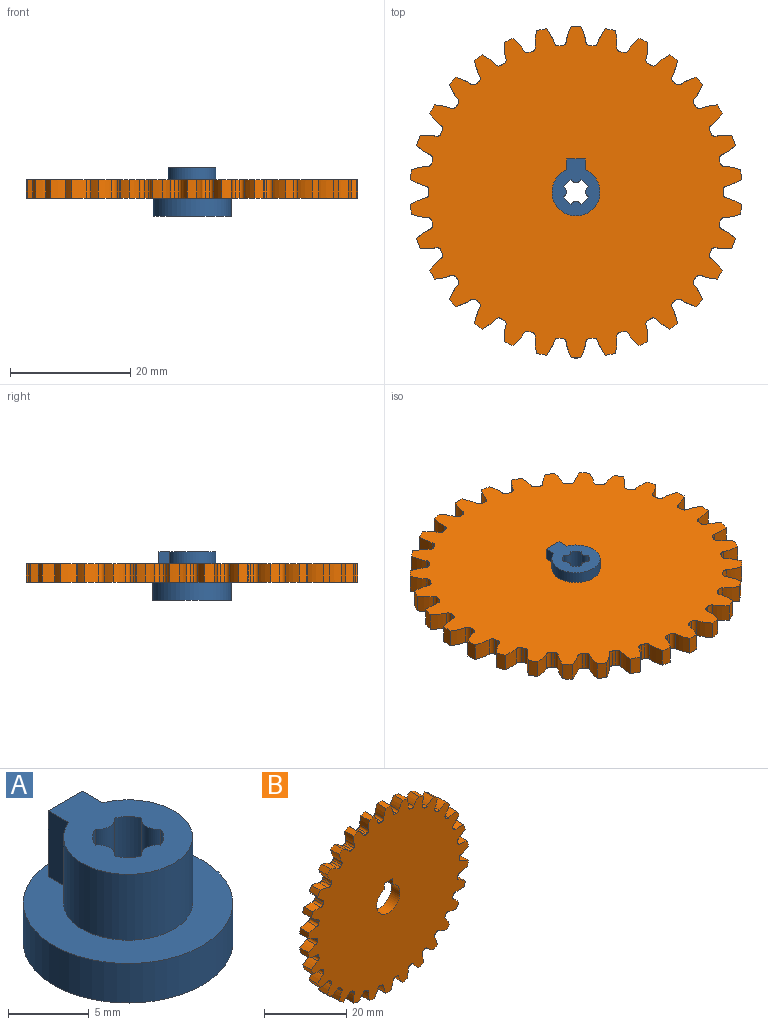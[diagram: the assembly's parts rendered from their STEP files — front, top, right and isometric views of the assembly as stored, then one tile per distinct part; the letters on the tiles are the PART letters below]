
ASSEMBLY  parts=2 mates=1
PART A: 18 faces, bbox 13x13x8 mm
  f0: cylinder r=2.2mm len=6mm, axis (0,0,-1), area 10.6mm2, adj f11,f13,f14,f17
  f1: cylinder r=2.2mm len=6mm, axis (0,0,-1), area 10.6mm2, adj f11,f13,f16,f17
  f2: cylinder r=2.2mm len=6mm, axis (0,0,-1), area 10.6mm2, adj f11,f13,f15,f16
  f3: cylinder r=2.2mm len=6mm, axis (0,0,-1), area 10.6mm2, adj f11,f13,f14,f15
  f4: cylinder r=6.5mm len=13mm, axis (0,0,-1), area 122.5mm2, adj f5,f6
  f5: plane 13x13mm, normal (0,0,1), area 77.7mm2, adj f4,f7,f8,f9,f10
  f6: plane 13x13mm, normal (0,0,-1), area 99.5mm2, adj f4,f12
  f7: cylinder r=4mm len=8mm, axis (0,0,-1), area 110.3mm2, adj f5,f8,f10,f11
  f8: plane 5x1.79mm, normal (1,0,0), area 9mm2, adj f5,f7,f9,f11
  f9: plane 5x3mm, normal (0,1,0), area 15mm2, adj f5,f8,f10,f11
  f10: plane 5x1.79mm, normal (-1,0,0), area 9mm2, adj f5,f7,f9,f11
  f11: plane 9.5x8mm, normal (0,0,1), area 42.6mm2, adj f0,f1,f2,f3,f7,f8,f9,f10
  f12: cylinder r=3.25mm len=6.5mm, axis (0,0,1), area 40.8mm2, adj f6,f13
  f13: plane 6.5x6.5mm, normal (0,0,-1), area 20.7mm2, adj f0,f1,f2,f3,f12,f14,f15,f16
  f14: cylinder r=1mm len=6mm, axis (0,0,1), area 11.7mm2, adj f0,f3,f11,f13
  f15: cylinder r=1mm len=6mm, axis (0,0,1), area 11.7mm2, adj f2,f3,f11,f13
  f16: cylinder r=1mm len=6mm, axis (0,0,1), area 11.7mm2, adj f1,f2,f11,f13
  f17: cylinder r=1mm len=6mm, axis (0,0,1), area 11.7mm2, adj f0,f1,f11,f13
PART B: 186 faces, bbox 55.1x3x55.3 mm
  f0: cylinder r=27.65mm len=3mm, axis (0,1,0), area 4.9mm2, adj f29,f35,f36,f183
  f1: cylinder r=27.65mm len=3mm, axis (0,1,0), area 4.9mm2, adj f29,f35,f178,f181
  f2: cylinder r=27.65mm len=3mm, axis (0,1,0), area 4.9mm2, adj f29,f35,f166,f173
  f3: cylinder r=27.65mm len=3mm, axis (0,1,0), area 4.9mm2, adj f29,f35,f168,f176
  f4: cylinder r=27.65mm len=3mm, axis (0,1,0), area 4.9mm2, adj f29,f35,f163,f171
  f5: cylinder r=27.65mm len=3mm, axis (0,1,0), area 4.9mm2, adj f29,f35,f158,f161
  f6: cylinder r=27.65mm len=3mm, axis (0,1,0), area 4.9mm2, adj f29,f35,f153,f156
  f7: cylinder r=27.65mm len=3mm, axis (0,1,0), area 4.9mm2, adj f29,f35,f148,f151
  f8: cylinder r=27.65mm len=3mm, axis (0,1,0), area 4.9mm2, adj f29,f35,f143,f146
  f9: cylinder r=27.65mm len=3mm, axis (0,1,0), area 4.9mm2, adj f29,f35,f138,f141
  f10: cylinder r=27.65mm len=3mm, axis (0,1,0), area 4.9mm2, adj f29,f35,f126,f133
  f11: cylinder r=27.65mm len=3mm, axis (0,1,0), area 4.9mm2, adj f29,f35,f128,f136
  f12: cylinder r=27.65mm len=3mm, axis (0,1,0), area 4.9mm2, adj f29,f35,f123,f131
  f13: cylinder r=27.65mm len=3mm, axis (0,1,0), area 4.9mm2, adj f29,f35,f118,f121
  f14: cylinder r=27.65mm len=3mm, axis (0,1,0), area 4.9mm2, adj f29,f35,f113,f116
  f15: cylinder r=27.65mm len=3mm, axis (0,1,0), area 4.9mm2, adj f29,f35,f108,f111
  f16: cylinder r=27.65mm len=3mm, axis (0,1,0), area 4.9mm2, adj f29,f35,f96,f103
  f17: cylinder r=27.65mm len=3mm, axis (0,1,0), area 4.9mm2, adj f29,f35,f91,f98
  f18: cylinder r=27.65mm len=3mm, axis (0,1,0), area 4.9mm2, adj f29,f35,f86,f93
  f19: cylinder r=27.65mm len=3mm, axis (0,1,0), area 4.9mm2, adj f29,f35,f88,f106
  f20: cylinder r=27.65mm len=3mm, axis (0,1,0), area 4.9mm2, adj f29,f35,f83,f101
  f21: cylinder r=27.65mm len=3mm, axis (0,1,0), area 4.9mm2, adj f29,f35,f78,f81
  f22: cylinder r=27.65mm len=3mm, axis (0,1,0), area 4.9mm2, adj f29,f35,f73,f76
  f23: cylinder r=27.65mm len=3mm, axis (0,1,0), area 4.9mm2, adj f29,f35,f68,f71
  f24: cylinder r=27.65mm len=3mm, axis (0,1,0), area 4.9mm2, adj f29,f35,f56,f63
  f25: cylinder r=27.65mm len=3mm, axis (0,1,0), area 4.9mm2, adj f29,f35,f51,f58
  f26: cylinder r=27.65mm len=3mm, axis (0,1,0), area 4.9mm2, adj f29,f35,f46,f53
  f27: cylinder r=27.65mm len=3mm, axis (0,1,0), area 4.9mm2, adj f29,f35,f48,f66
  f28: cylinder r=27.65mm len=3mm, axis (0,1,0), area 4.9mm2, adj f29,f35,f43,f61
  f29: plane 55.3x55.15mm, normal (0,-1,0), area 2093.7mm2, adj f0,f1,f2,f3,f4,f5,f6,f7
  f30: plane 3x1.79mm, normal (-1,0,0), area 5.4mm2, adj f29,f31,f33,f35
  f31: cylinder r=4mm len=8mm, axis (0,1,0), area 66.2mm2, adj f29,f30,f32,f35
  f32: plane 3x1.79mm, normal (1,0,0), area 5.4mm2, adj f29,f31,f33,f35
  f33: plane 3x3mm, normal (0,0,-1), area 9mm2, adj f29,f30,f32,f35
  f34: cylinder r=27.65mm len=3mm, axis (0,1,0), area 4.9mm2, adj f29,f35,f38,f41
  f35: plane 55.3x55.15mm, normal (0,1,0), area 2093.7mm2, adj f0,f1,f2,f3,f4,f5,f6,f7
  f36: extruded ~3x2.51mm, area 8.2mm2, adj f0,f29,f35,f39
  f37: cylinder r=24.5mm len=3mm, axis (0,1,0), area 1.6mm2, adj f29,f35,f39,f40
  f38: extruded ~3x2.51mm, area 8.2mm2, adj f29,f34,f35,f40
  f39: cylinder r=0.73mm len=3mm, axis (0,1,0), area 3mm2, adj f29,f35,f36,f37
  f40: cylinder r=0.73mm len=3mm, axis (0,1,0), area 3mm2, adj f29,f35,f37,f38
  f41: extruded ~3x2.68mm, area 8.2mm2, adj f29,f34,f35,f44
  f42: cylinder r=24.5mm len=3mm, axis (0,1,0), area 1.6mm2, adj f29,f35,f44,f45
  f43: extruded ~3x2.23mm, area 8.2mm2, adj f28,f29,f35,f45
  f44: cylinder r=0.73mm len=3mm, axis (0,1,0), area 3mm2, adj f29,f35,f41,f42
  f45: cylinder r=0.73mm len=3mm, axis (0,1,0), area 3mm2, adj f29,f35,f42,f43
  f46: extruded ~3x2.19mm, area 8.2mm2, adj f26,f29,f35,f49
  f47: cylinder r=24.5mm len=3mm, axis (0,1,0), area 1.6mm2, adj f29,f35,f49,f50
  f48: extruded ~3x2.71mm, area 8.2mm2, adj f27,f29,f35,f50
  f49: cylinder r=0.73mm len=3mm, axis (0,1,0), area 3mm2, adj f29,f35,f46,f47
  f50: cylinder r=0.73mm len=3mm, axis (0,1,0), area 3mm2, adj f29,f35,f47,f48
  f51: extruded ~3x2.48mm, area 8.2mm2, adj f25,f29,f35,f54
  f52: cylinder r=24.5mm len=3mm, axis (0,1,0), area 1.6mm2, adj f29,f35,f54,f55
  f53: extruded ~3x2.59mm, area 8.2mm2, adj f26,f29,f35,f55
  f54: cylinder r=0.73mm len=3mm, axis (0,1,0), area 3mm2, adj f29,f35,f51,f52
  f55: cylinder r=0.73mm len=3mm, axis (0,1,0), area 3mm2, adj f29,f35,f52,f53
  f56: extruded ~3x2.67mm, area 8.2mm2, adj f24,f29,f35,f59
  f57: cylinder r=24.5mm len=3mm, axis (0,1,0), area 1.6mm2, adj f29,f35,f59,f60
  f58: extruded ~3x2.35mm, area 8.2mm2, adj f25,f29,f35,f60
  f59: cylinder r=0.73mm len=3mm, axis (0,1,0), area 3mm2, adj f29,f35,f56,f57
  f60: cylinder r=0.73mm len=3mm, axis (0,1,0), area 3mm2, adj f29,f35,f57,f58
  f61: extruded ~3x2.73mm, area 8.2mm2, adj f28,f29,f35,f64
  f62: cylinder r=24.5mm len=3mm, axis (0,1,0), area 1.6mm2, adj f29,f35,f64,f65
  f63: extruded ~3x2.01mm, area 8.2mm2, adj f24,f29,f35,f65
  f64: cylinder r=0.73mm len=3mm, axis (0,1,0), area 3mm2, adj f29,f35,f61,f62
  f65: cylinder r=0.73mm len=3mm, axis (0,1,0), area 3mm2, adj f29,f35,f62,f63
  f66: extruded ~3x2.05mm, area 8.2mm2, adj f27,f29,f35,f69
  f67: cylinder r=24.5mm len=3mm, axis (0,1,0), area 1.6mm2, adj f29,f35,f69,f70
  f68: extruded ~3x2.72mm, area 8.2mm2, adj f23,f29,f35,f70
  f69: cylinder r=0.73mm len=3mm, axis (0,1,0), area 3mm2, adj f29,f35,f66,f67
  f70: cylinder r=0.73mm len=3mm, axis (0,1,0), area 3mm2, adj f29,f35,f67,f68
  f71: extruded ~3x2.38mm, area 8.2mm2, adj f23,f29,f35,f74
  f72: cylinder r=24.5mm len=3mm, axis (0,1,0), area 1.6mm2, adj f29,f35,f74,f75
  f73: extruded ~3x2.61mm, area 8.2mm2, adj f22,f29,f35,f75
  f74: cylinder r=0.73mm len=3mm, axis (0,1,0), area 3mm2, adj f29,f35,f71,f72
  f75: cylinder r=0.73mm len=3mm, axis (0,1,0), area 3mm2, adj f29,f35,f72,f73
  f76: extruded ~3x2.61mm, area 8.2mm2, adj f22,f29,f35,f79
  f77: cylinder r=24.5mm len=3mm, axis (0,1,0), area 1.6mm2, adj f29,f35,f79,f80
  f78: extruded ~3x2.38mm, area 8.2mm2, adj f21,f29,f35,f80
  f79: cylinder r=0.73mm len=3mm, axis (0,1,0), area 3mm2, adj f29,f35,f76,f77
  f80: cylinder r=0.73mm len=3mm, axis (0,1,0), area 3mm2, adj f29,f35,f77,f78
  f81: extruded ~3x2.72mm, area 8.2mm2, adj f21,f29,f35,f84
  f82: cylinder r=24.5mm len=3mm, axis (0,1,0), area 1.6mm2, adj f29,f35,f84,f85
  f83: extruded ~3x2.05mm, area 8.2mm2, adj f20,f29,f35,f85
  f84: cylinder r=0.73mm len=3mm, axis (0,1,0), area 3mm2, adj f29,f35,f81,f82
  f85: cylinder r=0.73mm len=3mm, axis (0,1,0), area 3mm2, adj f29,f35,f82,f83
  f86: extruded ~3x2.01mm, area 8.2mm2, adj f18,f29,f35,f89
  f87: cylinder r=24.5mm len=3mm, axis (0,1,0), area 1.6mm2, adj f29,f35,f89,f90
  f88: extruded ~3x2.73mm, area 8.2mm2, adj f19,f29,f35,f90
  f89: cylinder r=0.73mm len=3mm, axis (0,1,0), area 3mm2, adj f29,f35,f86,f87
  f90: cylinder r=0.73mm len=3mm, axis (0,1,0), area 3mm2, adj f29,f35,f87,f88
  f91: extruded ~3x2.35mm, area 8.2mm2, adj f17,f29,f35,f94
  f92: cylinder r=24.5mm len=3mm, axis (0,1,0), area 1.6mm2, adj f29,f35,f94,f95
  f93: extruded ~3x2.67mm, area 8.2mm2, adj f18,f29,f35,f95
  f94: cylinder r=0.73mm len=3mm, axis (0,1,0), area 3mm2, adj f29,f35,f91,f92
  f95: cylinder r=0.73mm len=3mm, axis (0,1,0), area 3mm2, adj f29,f35,f92,f93
  f96: extruded ~3x2.59mm, area 8.2mm2, adj f16,f29,f35,f99
  f97: cylinder r=24.5mm len=3mm, axis (0,1,0), area 1.6mm2, adj f29,f35,f99,f100
  f98: extruded ~3x2.48mm, area 8.2mm2, adj f17,f29,f35,f100
  f99: cylinder r=0.73mm len=3mm, axis (0,1,0), area 3mm2, adj f29,f35,f96,f97
  f100: cylinder r=0.73mm len=3mm, axis (0,1,0), area 3mm2, adj f29,f35,f97,f98
  f101: extruded ~3x2.71mm, area 8.2mm2, adj f20,f29,f35,f104
  f102: cylinder r=24.5mm len=3mm, axis (0,1,0), area 1.6mm2, adj f29,f35,f104,f105
  f103: extruded ~3x2.19mm, area 8.2mm2, adj f16,f29,f35,f105
  f104: cylinder r=0.73mm len=3mm, axis (0,1,0), area 3mm2, adj f29,f35,f101,f102
  f105: cylinder r=0.73mm len=3mm, axis (0,1,0), area 3mm2, adj f29,f35,f102,f103
  f106: extruded ~3x2.23mm, area 8.2mm2, adj f19,f29,f35,f109
  f107: cylinder r=24.5mm len=3mm, axis (0,1,0), area 1.6mm2, adj f29,f35,f109,f110
  f108: extruded ~3x2.68mm, area 8.2mm2, adj f15,f29,f35,f110
  f109: cylinder r=0.73mm len=3mm, axis (0,1,0), area 3mm2, adj f29,f35,f106,f107
  f110: cylinder r=0.73mm len=3mm, axis (0,1,0), area 3mm2, adj f29,f35,f107,f108
  f111: extruded ~3x2.51mm, area 8.2mm2, adj f15,f29,f35,f114
  f112: cylinder r=24.5mm len=3mm, axis (0,1,0), area 1.6mm2, adj f29,f35,f114,f115
  f113: extruded ~3x2.51mm, area 8.2mm2, adj f14,f29,f35,f115
  f114: cylinder r=0.73mm len=3mm, axis (0,1,0), area 3mm2, adj f29,f35,f111,f112
  f115: cylinder r=0.73mm len=3mm, axis (0,1,0), area 3mm2, adj f29,f35,f112,f113
  f116: extruded ~3x2.68mm, area 8.2mm2, adj f14,f29,f35,f119
  f117: cylinder r=24.5mm len=3mm, axis (0,1,0), area 1.6mm2, adj f29,f35,f119,f120
  f118: extruded ~3x2.23mm, area 8.2mm2, adj f13,f29,f35,f120
  f119: cylinder r=0.73mm len=3mm, axis (0,1,0), area 3mm2, adj f29,f35,f116,f117
  f120: cylinder r=0.73mm len=3mm, axis (0,1,0), area 3mm2, adj f29,f35,f117,f118
  f121: extruded ~3x2.73mm, area 8.2mm2, adj f13,f29,f35,f124
  f122: cylinder r=24.5mm len=3mm, axis (0,1,0), area 1.6mm2, adj f29,f35,f124,f125
  f123: extruded ~3x2.01mm, area 8.2mm2, adj f12,f29,f35,f125
  f124: cylinder r=0.73mm len=3mm, axis (0,1,0), area 3mm2, adj f29,f35,f121,f122
  f125: cylinder r=0.73mm len=3mm, axis (0,1,0), area 3mm2, adj f29,f35,f122,f123
  f126: extruded ~3x2.48mm, area 8.2mm2, adj f10,f29,f35,f129
  f127: cylinder r=24.5mm len=3mm, axis (0,1,0), area 1.6mm2, adj f29,f35,f129,f130
  f128: extruded ~3x2.59mm, area 8.2mm2, adj f11,f29,f35,f130
  f129: cylinder r=0.73mm len=3mm, axis (0,1,0), area 3mm2, adj f29,f35,f126,f127
  f130: cylinder r=0.73mm len=3mm, axis (0,1,0), area 3mm2, adj f29,f35,f127,f128
  f131: extruded ~3x2.67mm, area 8.2mm2, adj f12,f29,f35,f134
  f132: cylinder r=24.5mm len=3mm, axis (0,1,0), area 1.6mm2, adj f29,f35,f134,f135
  f133: extruded ~3x2.35mm, area 8.2mm2, adj f10,f29,f35,f135
  f134: cylinder r=0.73mm len=3mm, axis (0,1,0), area 3mm2, adj f29,f35,f131,f132
  f135: cylinder r=0.73mm len=3mm, axis (0,1,0), area 3mm2, adj f29,f35,f132,f133
  f136: extruded ~3x2.19mm, area 8.2mm2, adj f11,f29,f35,f139
  f137: cylinder r=24.5mm len=3mm, axis (0,1,0), area 1.6mm2, adj f29,f35,f139,f140
  f138: extruded ~3x2.71mm, area 8.2mm2, adj f9,f29,f35,f140
  f139: cylinder r=0.73mm len=3mm, axis (0,1,0), area 3mm2, adj f29,f35,f136,f137
  f140: cylinder r=0.73mm len=3mm, axis (0,1,0), area 3mm2, adj f29,f35,f137,f138
  f141: extruded ~3x2.05mm, area 8.2mm2, adj f9,f29,f35,f144
  f142: cylinder r=24.5mm len=3mm, axis (0,1,0), area 1.6mm2, adj f29,f35,f144,f145
  f143: extruded ~3x2.72mm, area 8.2mm2, adj f8,f29,f35,f145
  f144: cylinder r=0.73mm len=3mm, axis (0,1,0), area 3mm2, adj f29,f35,f141,f142
  f145: cylinder r=0.73mm len=3mm, axis (0,1,0), area 3mm2, adj f29,f35,f142,f143
  f146: extruded ~3x2.38mm, area 8.2mm2, adj f8,f29,f35,f149
  f147: cylinder r=24.5mm len=3mm, axis (0,1,0), area 1.6mm2, adj f29,f35,f149,f150
  f148: extruded ~3x2.61mm, area 8.2mm2, adj f7,f29,f35,f150
  f149: cylinder r=0.73mm len=3mm, axis (0,1,0), area 3mm2, adj f29,f35,f146,f147
  f150: cylinder r=0.73mm len=3mm, axis (0,1,0), area 3mm2, adj f29,f35,f147,f148
  f151: extruded ~3x2.61mm, area 8.2mm2, adj f7,f29,f35,f154
  f152: cylinder r=24.5mm len=3mm, axis (0,1,0), area 1.6mm2, adj f29,f35,f154,f155
  f153: extruded ~3x2.38mm, area 8.2mm2, adj f6,f29,f35,f155
  f154: cylinder r=0.73mm len=3mm, axis (0,1,0), area 3mm2, adj f29,f35,f151,f152
  f155: cylinder r=0.73mm len=3mm, axis (0,1,0), area 3mm2, adj f29,f35,f152,f153
  f156: extruded ~3x2.72mm, area 8.2mm2, adj f6,f29,f35,f159
  f157: cylinder r=24.5mm len=3mm, axis (0,1,0), area 1.6mm2, adj f29,f35,f159,f160
  f158: extruded ~3x2.05mm, area 8.2mm2, adj f5,f29,f35,f160
  f159: cylinder r=0.73mm len=3mm, axis (0,1,0), area 3mm2, adj f29,f35,f156,f157
  f160: cylinder r=0.73mm len=3mm, axis (0,1,0), area 3mm2, adj f29,f35,f157,f158
  f161: extruded ~3x2.71mm, area 8.2mm2, adj f5,f29,f35,f164
  f162: cylinder r=24.5mm len=3mm, axis (0,1,0), area 1.6mm2, adj f29,f35,f164,f165
  f163: extruded ~3x2.19mm, area 8.2mm2, adj f4,f29,f35,f165
  f164: cylinder r=0.73mm len=3mm, axis (0,1,0), area 3mm2, adj f29,f35,f161,f162
  f165: cylinder r=0.73mm len=3mm, axis (0,1,0), area 3mm2, adj f29,f35,f162,f163
  f166: extruded ~3x2.35mm, area 8.2mm2, adj f2,f29,f35,f169
  f167: cylinder r=24.5mm len=3mm, axis (0,1,0), area 1.6mm2, adj f29,f35,f169,f170
  f168: extruded ~3x2.67mm, area 8.2mm2, adj f3,f29,f35,f170
  f169: cylinder r=0.73mm len=3mm, axis (0,1,0), area 3mm2, adj f29,f35,f166,f167
  f170: cylinder r=0.73mm len=3mm, axis (0,1,0), area 3mm2, adj f29,f35,f167,f168
  f171: extruded ~3x2.59mm, area 8.2mm2, adj f4,f29,f35,f174
  f172: cylinder r=24.5mm len=3mm, axis (0,1,0), area 1.6mm2, adj f29,f35,f174,f175
  f173: extruded ~3x2.48mm, area 8.2mm2, adj f2,f29,f35,f175
  f174: cylinder r=0.73mm len=3mm, axis (0,1,0), area 3mm2, adj f29,f35,f171,f172
  f175: cylinder r=0.73mm len=3mm, axis (0,1,0), area 3mm2, adj f29,f35,f172,f173
  f176: extruded ~3x2.01mm, area 8.2mm2, adj f3,f29,f35,f179
  f177: cylinder r=24.5mm len=3mm, axis (0,1,0), area 1.6mm2, adj f29,f35,f179,f180
  f178: extruded ~3x2.73mm, area 8.2mm2, adj f1,f29,f35,f180
  f179: cylinder r=0.73mm len=3mm, axis (0,1,0), area 3mm2, adj f29,f35,f176,f177
  f180: cylinder r=0.73mm len=3mm, axis (0,1,0), area 3mm2, adj f29,f35,f177,f178
  f181: extruded ~3x2.23mm, area 8.2mm2, adj f1,f29,f35,f184
  f182: cylinder r=24.5mm len=3mm, axis (0,1,0), area 1.6mm2, adj f29,f35,f184,f185
  f183: extruded ~3x2.68mm, area 8.2mm2, adj f0,f29,f35,f185
  f184: cylinder r=0.73mm len=3mm, axis (0,1,0), area 3mm2, adj f29,f35,f181,f182
  f185: cylinder r=0.73mm len=3mm, axis (0,1,0), area 3mm2, adj f29,f35,f182,f183
PLACE A t=(-0.96,25.91,-24.41)mm
PLACE B rot(axis=(-1,0,0),90deg) t=(-0.96,25.91,-7.41)mm
MATE fastened B.f0 <-> A.f0  axis (0,0,-1) through (-0.96,25.91,-7.41)mm
